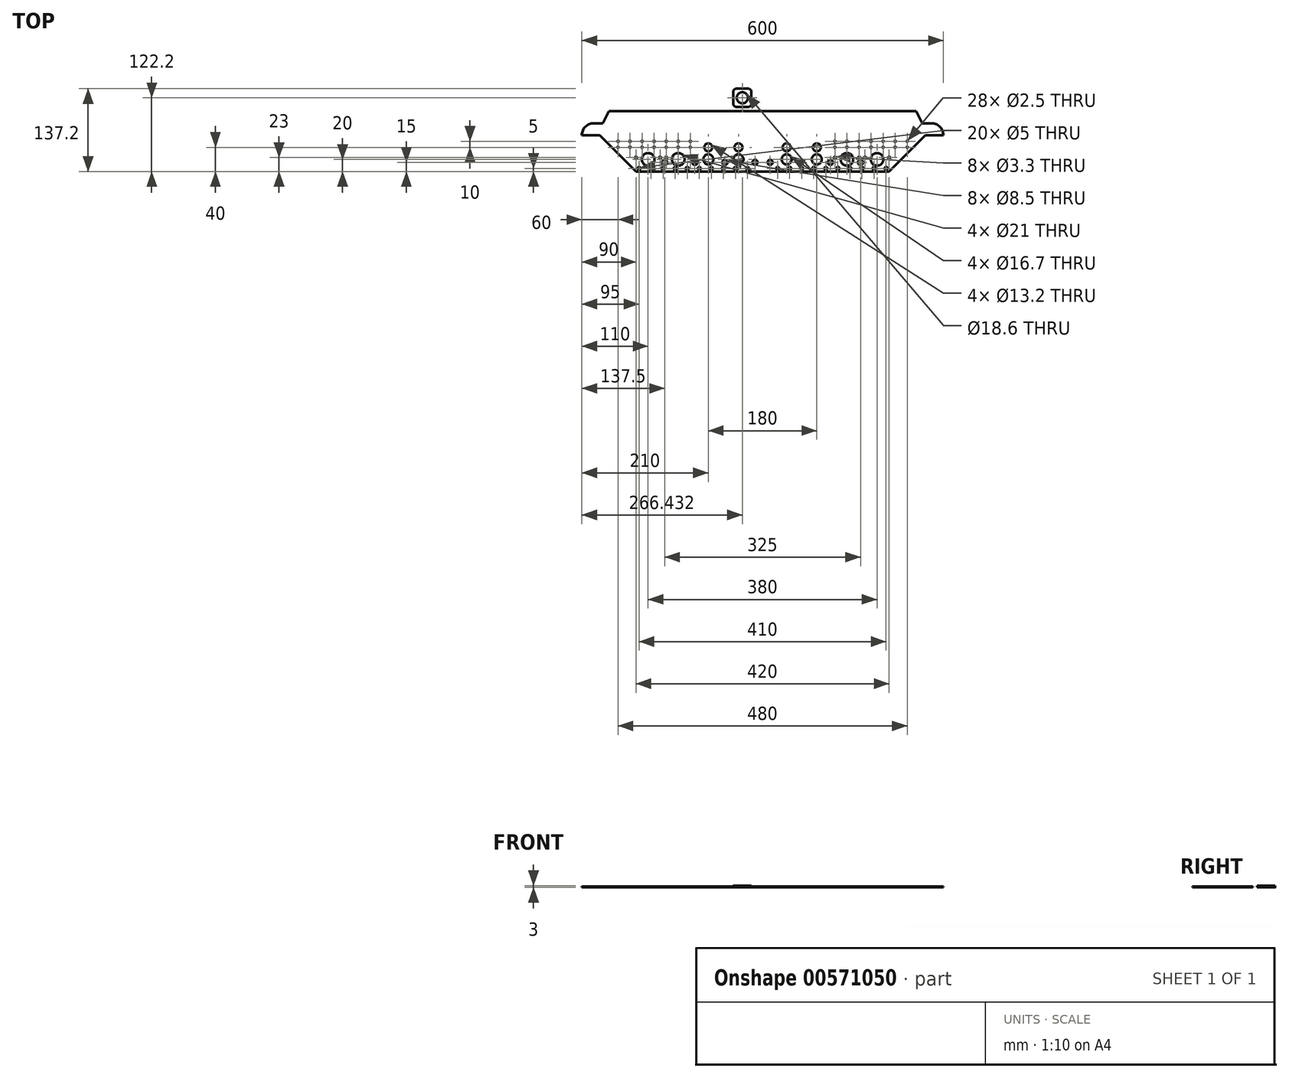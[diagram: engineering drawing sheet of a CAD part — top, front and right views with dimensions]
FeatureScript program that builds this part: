
annotation { "Feature Type Name" : "Feature", "Feature Type Description" : "" }
export const myFeature = defineFeature(function(context is Context, id is Id, definition is map)
    precondition{}
    {
        {
            var Q0;
            Q0=qCreatedBy(makeId("Top.planeOp"),FACE);
            var sketch = newSketch(context, id + "F0", { "sketchPlane" : qUnion([Q0])});
            skLineSegment(sketch, "E0", {"start": v(0, 0) * mm, "end": v(-255, 0) * mm});
            skLineSegment(sketch, "E1", {"start": v(-300, -40) * mm, "end": v(-270, -40) * mm});
            skLineSegment(sketch, "E2", {"start": v(-270, -40) * mm, "end": v(-210, -100) * mm});
            skLineSegment(sketch, "E3", {"start": v(-210, -100) * mm, "end": v(0, -100) * mm});
            skLineSegment(sketch, "E4", {"start": v(-255, 0) * mm, "end": v(-265, -20) * mm});
            skLineSegment(sketch, "E5", {"start": v(-265, -20) * mm, "end": v(-280, -20) * mm});
            skArc(sketch, "E6", {"start": v(-280, -20) * mm, "mid": v(-294.14, -25.86) * mm, "end": v(-300, -40) * mm});
            skCircle(sketch, "E7", {"center": v(-210, -77) * mm, "radius": 1.65 * mm});
            skCircle(sketch, "E8", {"center": v(-190, -80) * mm, "radius": 10.5 * mm});
            skCircle(sketch, "E9", {"center": v(-90, -80) * mm, "radius": 8.35 * mm});
            skCircle(sketch, "E10", {"center": v(-90, -60) * mm, "radius": 6.6 * mm});
            skCircle(sketch, "E11", {"center": v(-205, -95) * mm, "radius": 2.5 * mm});
            skCircle(sketch, "E12.1.0.0", {"center": v(-40, -80) * mm, "radius": 8.35 * mm});
            skLineSegment(sketch, "E12.direction1", {"start": v(-90, -80) * mm, "end": v(-40, -80) * mm, "construction": true});
            skCircle(sketch, "E13.1.0.0", {"center": v(-40, -60) * mm, "radius": 6.6 * mm});
            skLineSegment(sketch, "E13.direction1", {"start": v(-90, -60) * mm, "end": v(-40, -60) * mm, "construction": true});
            skCircle(sketch, "E14.1.0.0", {"center": v(-170, -77) * mm, "radius": 1.65 * mm});
            skLineSegment(sketch, "E14.direction1", {"start": v(-210, -77) * mm, "end": v(-170, -77) * mm, "construction": true});
            skCircle(sketch, "E15.1.0.0", {"center": v(-140, -80) * mm, "radius": 10.5 * mm});
            skLineSegment(sketch, "E15.1.0.1", {"start": v(-160, -77) * mm, "end": v(-120, -77) * mm, "construction": true});
            skCircle(sketch, "E15.1.0.2", {"center": v(-120, -77) * mm, "radius": 1.65 * mm});
            skCircle(sketch, "E15.1.0.3", {"center": v(-160, -77) * mm, "radius": 1.65 * mm});
            skLineSegment(sketch, "E15.direction1", {"start": v(-210, -77) * mm, "end": v(-160, -77) * mm, "construction": true});
            skCircle(sketch, "E16.1.0.0", {"center": v(-185, -95) * mm, "radius": 2.5 * mm});
            skCircle(sketch, "E16.2.0.0", {"center": v(-165, -95) * mm, "radius": 2.5 * mm});
            skCircle(sketch, "E16.3.0.0", {"center": v(-145, -95) * mm, "radius": 2.5 * mm});
            skCircle(sketch, "E16.4.0.0", {"center": v(-125, -95) * mm, "radius": 2.5 * mm});
            skCircle(sketch, "E16.5.0.0", {"center": v(-105, -95) * mm, "radius": 2.5 * mm});
            skCircle(sketch, "E16.6.0.0", {"center": v(-85, -95) * mm, "radius": 2.5 * mm});
            skCircle(sketch, "E16.7.0.0", {"center": v(-65, -95) * mm, "radius": 2.5 * mm});
            skCircle(sketch, "E16.8.0.0", {"center": v(-45, -95) * mm, "radius": 2.5 * mm});
            skCircle(sketch, "E16.9.0.0", {"center": v(-25, -95) * mm, "radius": 2.5 * mm});
            skLineSegment(sketch, "E16.direction1", {"start": v(-205, -95) * mm, "end": v(-185, -95) * mm, "construction": true});
            skCircle(sketch, "E17", {"center": v(-240, -50) * mm, "radius": 1.25 * mm});
            skCircle(sketch, "E18.0.1.0", {"center": v(-240, -60) * mm, "radius": 1.25 * mm});
            skCircle(sketch, "E18.1.0.0", {"center": v(-220, -50) * mm, "radius": 1.25 * mm});
            skCircle(sketch, "E18.1.1.0", {"center": v(-220, -60) * mm, "radius": 1.25 * mm});
            skCircle(sketch, "E18.2.0.0", {"center": v(-200, -50) * mm, "radius": 1.25 * mm});
            skCircle(sketch, "E18.2.1.0", {"center": v(-200, -60) * mm, "radius": 1.25 * mm});
            skCircle(sketch, "E18.3.0.0", {"center": v(-180, -50) * mm, "radius": 1.25 * mm});
            skCircle(sketch, "E18.3.1.0", {"center": v(-180, -60) * mm, "radius": 1.25 * mm});
            skCircle(sketch, "E18.4.0.0", {"center": v(-160, -50) * mm, "radius": 1.25 * mm});
            skCircle(sketch, "E18.4.1.0", {"center": v(-160, -60) * mm, "radius": 1.25 * mm});
            skCircle(sketch, "E18.5.0.0", {"center": v(-140, -50) * mm, "radius": 1.25 * mm});
            skCircle(sketch, "E18.5.1.0", {"center": v(-140, -60) * mm, "radius": 1.25 * mm});
            skCircle(sketch, "E18.6.0.0", {"center": v(-120, -50) * mm, "radius": 1.25 * mm});
            skCircle(sketch, "E18.6.1.0", {"center": v(-120, -60) * mm, "radius": 1.25 * mm});
            skLineSegment(sketch, "E18.direction1", {"start": v(-240, -50) * mm, "end": v(-220, -50) * mm, "construction": true});
            skLineSegment(sketch, "E18.direction2", {"start": v(-240, -50) * mm, "end": v(-240, -60) * mm, "construction": true});
            skCircle(sketch, "E19", {"center": v(-162.5, -85) * mm, "radius": 4.25 * mm});
            skCircle(sketch, "E20.1.0.0", {"center": v(-112.5, -85) * mm, "radius": 4.25 * mm});
            skCircle(sketch, "E20.2.0.0", {"center": v(-62.5, -85) * mm, "radius": 4.25 * mm});
            skCircle(sketch, "E20.3.0.0", {"center": v(-12.5, -85) * mm, "radius": 4.25 * mm});
            skLineSegment(sketch, "E20.direction1", {"start": v(-162.5, -85) * mm, "end": v(-112.5, -85) * mm, "construction": true});
            skCircle(sketch, "E21.MirrorC", {"center": v(165, -95) * mm, "radius": 2.5 * mm});
            skCircle(sketch, "E22.MirrorC", {"center": v(160, -77) * mm, "radius": 1.65 * mm});
            skCircle(sketch, "E23.MirrorC", {"center": v(240, -50) * mm, "radius": 1.25 * mm});
            skCircle(sketch, "E24.MirrorC", {"center": v(220, -50) * mm, "radius": 1.25 * mm});
            skCircle(sketch, "E25.MirrorC", {"center": v(170, -77) * mm, "radius": 1.65 * mm});
            skCircle(sketch, "E26.MirrorC", {"center": v(180, -60) * mm, "radius": 1.25 * mm});
            skLineSegment(sketch, "E27.MirrorCS", {"start": v(240, -50) * mm, "end": v(240, -60) * mm, "construction": true});
            skCircle(sketch, "E28.MirrorC", {"center": v(145, -95) * mm, "radius": 2.5 * mm});
            skCircle(sketch, "E29.MirrorC", {"center": v(120, -77) * mm, "radius": 1.65 * mm});
            skCircle(sketch, "E30.MirrorC", {"center": v(220, -60) * mm, "radius": 1.25 * mm});
            skCircle(sketch, "E31.MirrorC", {"center": v(190, -80) * mm, "radius": 10.5 * mm});
            skCircle(sketch, "E32.MirrorC", {"center": v(200, -50) * mm, "radius": 1.25 * mm});
            skCircle(sketch, "E33.MirrorC", {"center": v(160, -60) * mm, "radius": 1.25 * mm});
            skCircle(sketch, "E34.MirrorC", {"center": v(240, -60) * mm, "radius": 1.25 * mm});
            skCircle(sketch, "E35.MirrorC", {"center": v(210, -77) * mm, "radius": 1.65 * mm});
            skCircle(sketch, "E36.MirrorC", {"center": v(200, -60) * mm, "radius": 1.25 * mm});
            skLineSegment(sketch, "E37.MirrorCS", {"start": v(240, -50) * mm, "end": v(220, -50) * mm, "construction": true});
            skCircle(sketch, "E38.MirrorC", {"center": v(162.5, -85) * mm, "radius": 4.25 * mm});
            skLineSegment(sketch, "E39.MirrorCS", {"start": v(210, -77) * mm, "end": v(160, -77) * mm, "construction": true});
            skCircle(sketch, "E40.MirrorC", {"center": v(180, -50) * mm, "radius": 1.25 * mm});
            skLineSegment(sketch, "E41.MirrorCS", {"start": v(210, -77) * mm, "end": v(170, -77) * mm, "construction": true});
            skCircle(sketch, "E42.MirrorC", {"center": v(140, -60) * mm, "radius": 1.25 * mm});
            skCircle(sketch, "E43.MirrorC", {"center": v(105, -95) * mm, "radius": 2.5 * mm});
            skCircle(sketch, "E44.MirrorC", {"center": v(160, -50) * mm, "radius": 1.25 * mm});
            skCircle(sketch, "E45.MirrorC", {"center": v(125, -95) * mm, "radius": 2.5 * mm});
            skCircle(sketch, "E46.MirrorC", {"center": v(140, -80) * mm, "radius": 10.5 * mm});
            skCircle(sketch, "E47.MirrorC", {"center": v(112.5, -85) * mm, "radius": 4.25 * mm});
            skCircle(sketch, "E48.MirrorC", {"center": v(140, -50) * mm, "radius": 1.25 * mm});
            skCircle(sketch, "E49.MirrorC", {"center": v(120, -50) * mm, "radius": 1.25 * mm});
            skLineSegment(sketch, "E50.MirrorCS", {"start": v(162.5, -85) * mm, "end": v(112.5, -85) * mm, "construction": true});
            skCircle(sketch, "E51.MirrorC", {"center": v(120, -60) * mm, "radius": 1.25 * mm});
            skCircle(sketch, "E52.MirrorC", {"center": v(205, -95) * mm, "radius": 2.5 * mm});
            skLineSegment(sketch, "E53.MirrorCS", {"start": v(160, -77) * mm, "end": v(120, -77) * mm, "construction": true});
            skLineSegment(sketch, "E54.MirrorCS", {"start": v(205, -95) * mm, "end": v(185, -95) * mm, "construction": true});
            skCircle(sketch, "E55.MirrorC", {"center": v(185, -95) * mm, "radius": 2.5 * mm});
            skCircle(sketch, "E56.MirrorC", {"center": v(65, -95) * mm, "radius": 2.5 * mm});
            skCircle(sketch, "E57.MirrorC", {"center": v(90, -80) * mm, "radius": 8.35 * mm});
            skCircle(sketch, "E58.MirrorC", {"center": v(90, -60) * mm, "radius": 6.6 * mm});
            skLineSegment(sketch, "E59.MirrorCS", {"start": v(90, -80) * mm, "end": v(40, -80) * mm, "construction": true});
            skLineSegment(sketch, "E60.MirrorCS", {"start": v(90, -60) * mm, "end": v(40, -60) * mm, "construction": true});
            skCircle(sketch, "E61.MirrorC", {"center": v(40, -60) * mm, "radius": 6.6 * mm});
            skCircle(sketch, "E62.MirrorC", {"center": v(45, -95) * mm, "radius": 2.5 * mm});
            skCircle(sketch, "E63.MirrorC", {"center": v(62.5, -85) * mm, "radius": 4.25 * mm});
            skCircle(sketch, "E64.MirrorC", {"center": v(85, -95) * mm, "radius": 2.5 * mm});
            skCircle(sketch, "E65.MirrorC", {"center": v(25, -95) * mm, "radius": 2.5 * mm});
            skLineSegment(sketch, "E66.MirrorCS", {"start": v(265, -20) * mm, "end": v(280, -20) * mm});
            skCircle(sketch, "E67.MirrorC", {"center": v(40, -80) * mm, "radius": 8.35 * mm});
            skLineSegment(sketch, "E68.MirrorCS", {"start": v(270, -40) * mm, "end": v(210, -100) * mm});
            skLineSegment(sketch, "E69.MirrorCS", {"start": v(300, -40) * mm, "end": v(270, -40) * mm});
            skArc(sketch, "E70.MirrorCS", {"start": v(280, -20) * mm, "mid": v(294.14, -25.86) * mm, "end": v(300, -40) * mm});
            skCircle(sketch, "E71.MirrorC", {"center": v(12.5, -85) * mm, "radius": 4.25 * mm});
            skLineSegment(sketch, "E72.MirrorCS", {"start": v(210, -100) * mm, "end": v(0, -100) * mm});
            skLineSegment(sketch, "E73.MirrorCS", {"start": v(255, 0) * mm, "end": v(265, -20) * mm});
            skLineSegment(sketch, "E74.MirrorCS", {"start": v(0, 0) * mm, "end": v(255, 0) * mm});
            skSolve(sketch);
        }
        {
            var Q0;
            Q0=makeQuery(id+"F0.imprint","IMPRINT",FACE,{"disambiguationData":[TD([[makeQuery(id+"F0.imprint","IMPRINT",EDGE,{"derivedFrom":sQuery(id+"F0.wireOp",EDGE,"E0")}),1.0]])]});
            extrude(context, id + "F1", {"entities" : qUnion([Q0]), "depth" : 1.5 * mm, "offsetDistance" : 25 * mm});
        }
        {
            var Q0;
            Q0=qCreatedBy(makeId("Top.planeOp"),FACE);
            var sketch = newSketch(context, id + "F2", { "sketchPlane" : qUnion([Q0])});
            skLineSegment(sketch, "E75", {"start": v(-48.57, 32.2) * mm, "end": v(-48.57, 22.2) * mm});
            skLineSegment(sketch, "E76", {"start": v(-43.57, 37.2) * mm, "end": v(-33.57, 37.2) * mm});
            skLineSegment(sketch, "E77", {"start": v(-33.57, 37.2) * mm, "end": v(-33.57, 22.2) * mm, "construction": true});
            skLineSegment(sketch, "E78", {"start": v(-33.57, 22.2) * mm, "end": v(-48.57, 22.2) * mm, "construction": true});
            skCircle(sketch, "E79", {"center": v(-33.57, 22.2) * mm, "radius": 9.3 * mm});
            skPoint(sketch, "E80.visualSharp", {"position": v(-48.57, 37.2) * mm});
            skArc(sketch, "E80.filletArc", {"start": v(-43.57, 37.2) * mm, "mid": v(-47.1, 35.74) * mm, "end": v(-48.57, 32.2) * mm});
            skLineSegment(sketch, "E81.1.0", {"start": v(-48.57, 12.2) * mm, "end": v(-48.57, 22.2) * mm});
            skPoint(sketch, "E81.1.1", {"position": v(-48.57, 7.2) * mm});
            skLineSegment(sketch, "E81.1.2", {"start": v(-33.57, 22.2) * mm, "end": v(-33.57, 7.2) * mm, "construction": true});
            skLineSegment(sketch, "E81.1.3", {"start": v(-43.57, 7.2) * mm, "end": v(-33.57, 7.2) * mm});
            skLineSegment(sketch, "E81.1.5", {"start": v(-48.57, 22.2) * mm, "end": v(-33.57, 22.2) * mm, "construction": true});
            skArc(sketch, "E81.1.6", {"start": v(-48.57, 12.2) * mm, "mid": v(-47.1, 8.66) * mm, "end": v(-43.57, 7.2) * mm});
            skLineSegment(sketch, "E81.2.0", {"start": v(-23.57, 7.2) * mm, "end": v(-33.57, 7.2) * mm});
            skPoint(sketch, "E81.2.1", {"position": v(-18.57, 7.2) * mm});
            skLineSegment(sketch, "E81.2.2", {"start": v(-33.57, 22.2) * mm, "end": v(-18.57, 22.2) * mm, "construction": true});
            skLineSegment(sketch, "E81.2.3", {"start": v(-18.57, 12.2) * mm, "end": v(-18.57, 22.2) * mm});
            skLineSegment(sketch, "E81.2.5", {"start": v(-33.57, 7.2) * mm, "end": v(-33.57, 22.2) * mm, "construction": true});
            skArc(sketch, "E81.2.6", {"start": v(-23.57, 7.2) * mm, "mid": v(-20.03, 8.66) * mm, "end": v(-18.57, 12.2) * mm});
            skLineSegment(sketch, "E81.3.0", {"start": v(-18.57, 32.2) * mm, "end": v(-18.57, 22.2) * mm});
            skPoint(sketch, "E81.3.1", {"position": v(-18.57, 37.2) * mm});
            skLineSegment(sketch, "E81.3.2", {"start": v(-33.57, 22.2) * mm, "end": v(-33.57, 37.2) * mm, "construction": true});
            skLineSegment(sketch, "E81.3.3", {"start": v(-23.57, 37.2) * mm, "end": v(-33.57, 37.2) * mm});
            skLineSegment(sketch, "E81.3.5", {"start": v(-18.57, 22.2) * mm, "end": v(-33.57, 22.2) * mm, "construction": true});
            skArc(sketch, "E81.3.6", {"start": v(-18.57, 32.2) * mm, "mid": v(-20.03, 35.74) * mm, "end": v(-23.57, 37.2) * mm});
            skSolve(sketch);
        }
        {
            var Q0;
            Q0=makeQuery(id+"F2.imprint","IMPRINT",FACE,{"disambiguationData":[TD([[makeQuery(id+"F2.imprint","IMPRINT",EDGE,{"derivedFrom":sQuery(id+"F2.wireOp",EDGE,"E75")}),1.0]])]});
            extrude(context, id + "F3", {"entities" : qUnion([Q0]), "depth" : 3 * mm, "offsetDistance" : 25 * mm});
        }
    });
